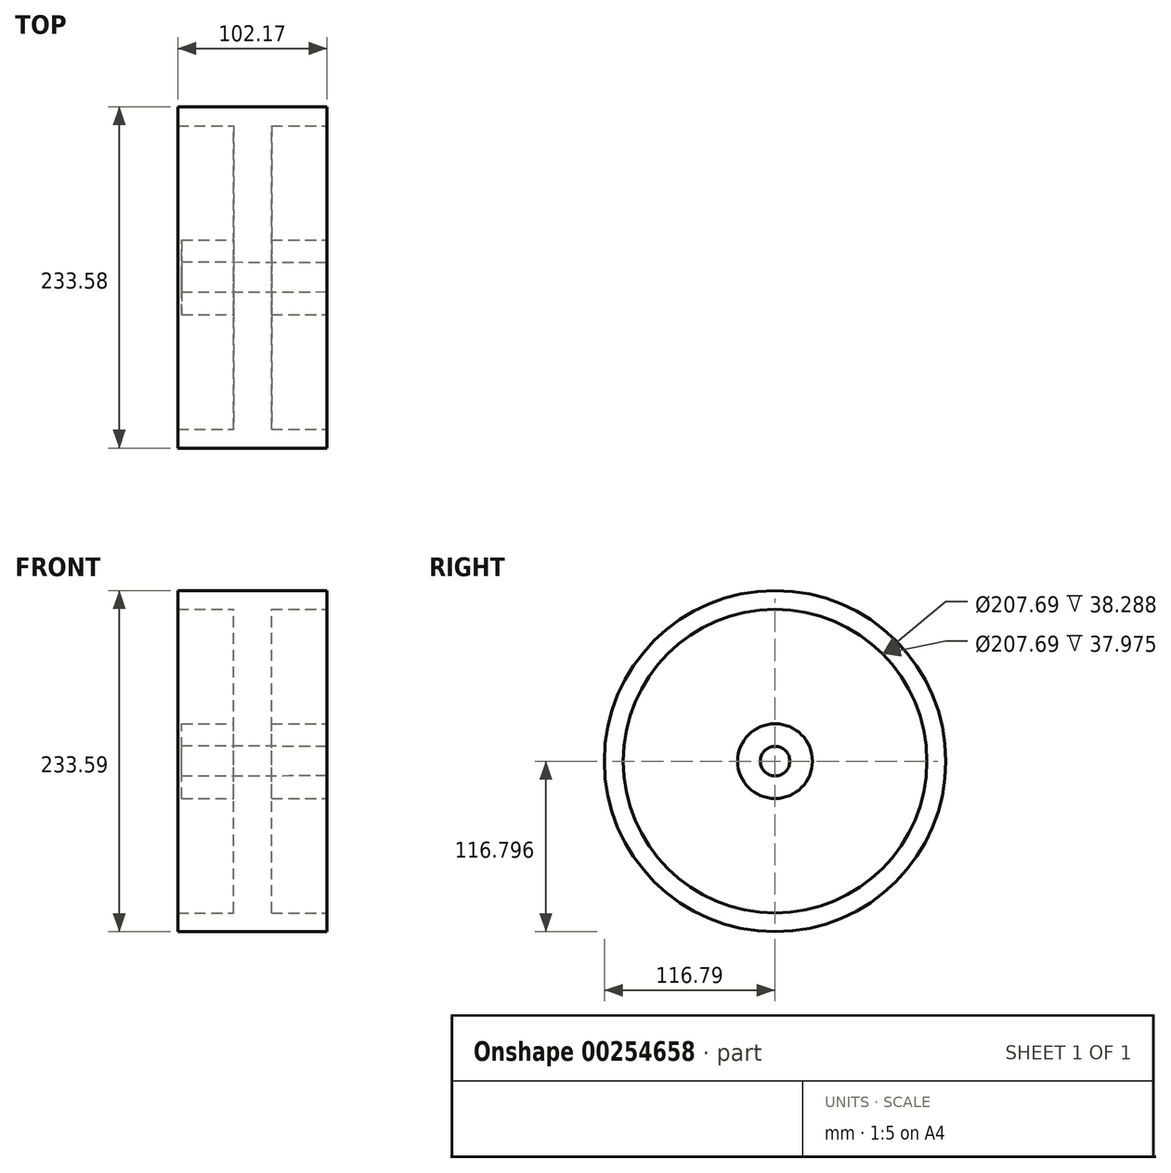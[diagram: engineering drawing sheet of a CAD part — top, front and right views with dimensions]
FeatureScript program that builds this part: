
annotation { "Feature Type Name" : "Feature", "Feature Type Description" : "" }
export const myFeature = defineFeature(function(context is Context, id is Id, definition is map)
    precondition{}
    {
        {
            var Q0;
            Q0=qCreatedBy(makeId("Front.planeOp"),FACE);
            var sketch = newSketch(context, id + "F0", { "sketchPlane" : qUnion([Q0])});
            skLineSegment(sketch, "E0", {"start": v(-51.23, 75.98) * mm, "end": v(50.94, 75.98) * mm});
            skLineSegment(sketch, "E1", {"start": v(-51.23, 75.98) * mm, "end": v(-51.23, 63.03) * mm});
            skLineSegment(sketch, "E2", {"start": v(50.94, 75.98) * mm, "end": v(50.94, 63.03) * mm});
            skLineSegment(sketch, "E3", {"start": v(-51.23, 63.03) * mm, "end": v(-12.94, 63.03) * mm});
            skLineSegment(sketch, "E4", {"start": v(50.94, 63.03) * mm, "end": v(12.97, 63.03) * mm});
            skLineSegment(sketch, "E5", {"start": v(-12.94, 63.03) * mm, "end": v(-12.94, -15.24) * mm});
            skLineSegment(sketch, "E6", {"start": v(12.97, 63.03) * mm, "end": v(12.97, -15.24) * mm});
            skLineSegment(sketch, "E7", {"start": v(-12.94, -15.24) * mm, "end": v(-48.5, -15.24) * mm});
            skLineSegment(sketch, "E8", {"start": v(12.97, -15.24) * mm, "end": v(50.81, -15.24) * mm});
            skLineSegment(sketch, "E9", {"start": v(-48.5, -15.24) * mm, "end": v(-48.5, -30.48) * mm});
            skLineSegment(sketch, "E10", {"start": v(50.81, -15.24) * mm, "end": v(50.81, -30.74) * mm});
            skLineSegment(sketch, "E11", {"start": v(-48.5, -30.48) * mm, "end": v(50.81, -30.74) * mm});
            skLineSegment(sketch, "E12", {"start": v(-83.75, -40.81) * mm, "end": v(77.99, -40.81) * mm, "construction": true});
            skSolve(sketch);
        }
        {
            var Q0;
            Q0=sQuery(id+"F0.wireOp",EDGE,"E1");
            var Q1;
            Q1=sQuery(id+"F0.wireOp",EDGE,"E3");
            var Q2;
            Q2=sQuery(id+"F0.wireOp",EDGE,"E5");
            var Q3;
            Q3=sQuery(id+"F0.wireOp",EDGE,"E9");
            var Q4;
            Q4=sQuery(id+"F0.wireOp",EDGE,"E7");
            var Q5;
            Q5=sQuery(id+"F0.wireOp",EDGE,"E11");
            var Q6;
            Q6=sQuery(id+"F0.wireOp",EDGE,"E10");
            var Q7;
            Q7=sQuery(id+"F0.wireOp",EDGE,"E8");
            var Q8;
            Q8=sQuery(id+"F0.wireOp",EDGE,"E6");
            var Q9;
            Q9=sQuery(id+"F0.wireOp",EDGE,"E4");
            var Q10;
            Q10=sQuery(id+"F0.wireOp",EDGE,"E0");
            var Q11;
            Q11=sQuery(id+"F0.wireOp",EDGE,"E2");
            var Q12;
            Q12=sQuery(id+"F0.wireOp",EDGE,"E12");
            revolve(context, id + "F1", {"bodyType" : ToolBodyType.SURFACE, "surfaceEntities" : qUnion([Q0, Q1, Q2, Q3, Q4, Q5, Q6, Q7, Q8, Q9, Q10, Q11]), "axis" : qUnion([Q12]), "revolveType" : RevolveType.FULL});
        }
    });
